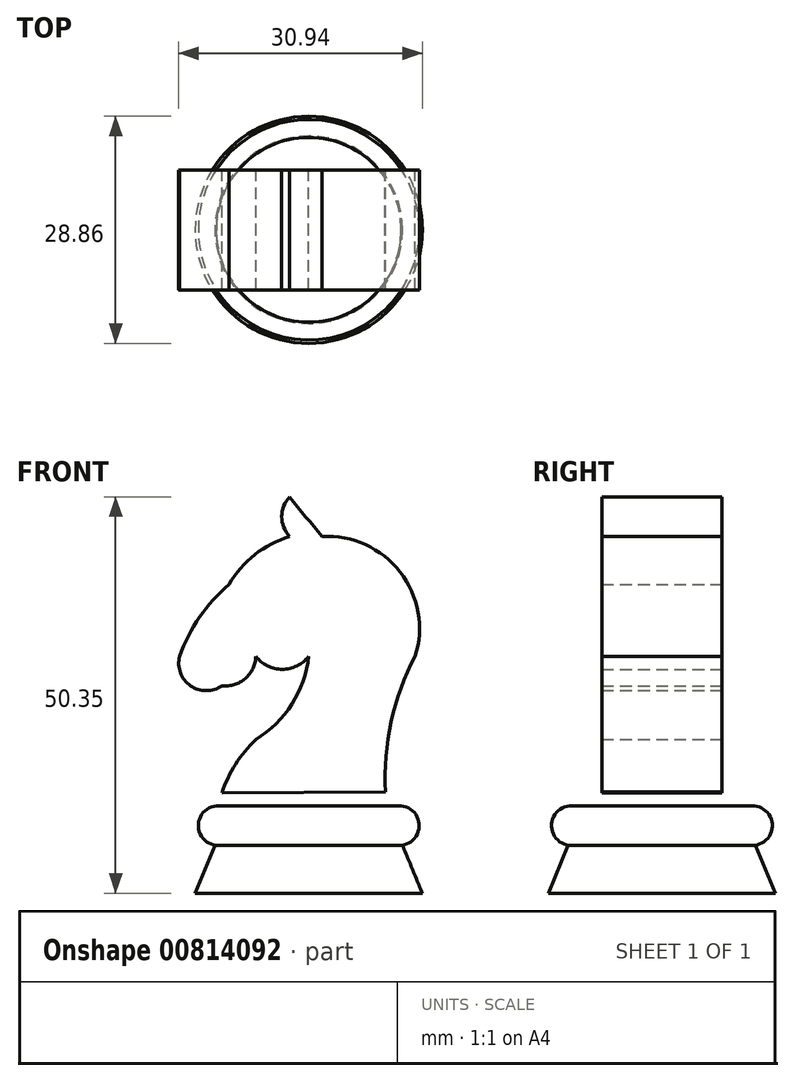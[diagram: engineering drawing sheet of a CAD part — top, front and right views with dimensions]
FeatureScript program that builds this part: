
annotation { "Feature Type Name" : "Feature", "Feature Type Description" : "" }
export const myFeature = defineFeature(function(context is Context, id is Id, definition is map)
    precondition{}
    {
        {
            var Q0;
            Q0=qCreatedBy(makeId("Front.planeOp"),FACE);
            var sketch = newSketch(context, id + "F0", { "sketchPlane" : qUnion([Q0])});
            skLineSegment(sketch, "E0", {"start": v(0, 0) * mm, "end": v(-14.43, 0) * mm});
            skLineSegment(sketch, "E1", {"start": v(-14.43, 0) * mm, "end": v(-11.92, 6.1) * mm});
            skLineSegment(sketch, "E2", {"start": v(-11.92, 6.1) * mm, "end": v(0, 6.1) * mm});
            skLineSegment(sketch, "E3", {"start": v(0, 6.1) * mm, "end": v(0, 0) * mm});
            skSolve(sketch);
        }
        {
            var Q0;
            Q0 = qSketchRegion(id + "F0", true);
            var Q1;
            Q1=sQuery(id+"F0.wireOp",EDGE,"E3");
            revolve(context, id + "F1", {"surfaceOperationType" : NewSurfaceOperationType.NEW, "entities" : qUnion([Q0]), "axis" : qUnion([Q1]), "revolveType" : RevolveType.FULL});
        }
        {
            var Q0;
            Q0=qCreatedBy(makeId("Front.planeOp"),FACE);
            var sketch = newSketch(context, id + "F2", { "sketchPlane" : qUnion([Q0])});
            skArc(sketch, "E4", {"start": v(-11.74, 11.11) * mm, "mid": v(-14, 8.33) * mm, "end": v(-11.2, 6.1) * mm});
            skLineSegment(sketch, "E5", {"start": v(-11.74, 11.11) * mm, "end": v(0, 11.11) * mm});
            skLineSegment(sketch, "E6", {"start": v(0, 11.11) * mm, "end": v(0, 5.73) * mm});
            skLineSegment(sketch, "E7", {"start": v(0, 5.73) * mm, "end": v(-11.2, 6.1) * mm});
            skSolve(sketch);
        }
        {
            var Q0;
            Q0 = qSketchRegion(id + "F2", true);
            var Q1;
            Q1=sQuery(id+"F2.wireOp",EDGE,"E6");
            revolve(context, id + "F3", {"operationType" : NewBodyOperationType.ADD, "surfaceOperationType" : NewSurfaceOperationType.NEW, "entities" : qUnion([Q0]), "axis" : qUnion([Q1]), "revolveType" : RevolveType.FULL});
        }
        {
            var Q0;
            Q0=qCreatedBy(makeId("Front.planeOp"),FACE);
            var sketch = newSketch(context, id + "F4", { "sketchPlane" : qUnion([Q0])});
            skArc(sketch, "E8", {"start": v(13.53, 30.1) * mm, "mid": v(10.47, 21.76) * mm, "end": v(9.77, 12.9) * mm});
            skArc(sketch, "E9", {"start": v(13.53, 30.1) * mm, "mid": v(11.6, 40.81) * mm, "end": v(1.7, 45.34) * mm});
            skArc(sketch, "E10", {"start": v(-2.42, 50.35) * mm, "mid": v(-0.38, 47.83) * mm, "end": v(1.7, 45.34) * mm});
            skArc(sketch, "E11", {"start": v(-2.42, 50.35) * mm, "mid": v(-3.43, 47.84) * mm, "end": v(-2.42, 45.34) * mm});
            skArc(sketch, "E12", {"start": v(-2.42, 45.34) * mm, "mid": v(-6.85, 43.01) * mm, "end": v(-10.12, 39.24) * mm});
            skArc(sketch, "E13", {"start": v(-10.12, 39.24) * mm, "mid": v(-13.85, 35.08) * mm, "end": v(-16.4, 30.1) * mm});
            skArc(sketch, "E14", {"start": v(-16.4, 30.1) * mm, "mid": v(-15, 26.36) * mm, "end": v(-11.02, 26.37) * mm});
            skArc(sketch, "E15", {"start": v(-11.02, 26.37) * mm, "mid": v(-8.04, 27.29) * mm, "end": v(-6.72, 30.1) * mm});
            skArc(sketch, "E16", {"start": v(-6.72, 30.1) * mm, "mid": v(-3.36, 28.45) * mm, "end": v(0, 30.1) * mm});
            skArc(sketch, "E17", {"start": v(-6.72, 19.53) * mm, "mid": v(-2.13, 24.04) * mm, "end": v(0, 30.1) * mm});
            skArc(sketch, "E18", {"start": v(-6.72, 19.53) * mm, "mid": v(-9.29, 16.4) * mm, "end": v(-11.02, 12.72) * mm});
            skLineSegment(sketch, "E19", {"start": v(-11.02, 12.72) * mm, "end": v(9.77, 12.9) * mm});
            skSolve(sketch);
        }
        {
            var Q0;
            Q0 = qSketchRegion(id + "F4", true);
            extrude(context, id + "F5", {"entities" : qUnion([Q0]), "depth" : 7.62 * mm, "offsetDistance" : 25.4 * mm});
        }
        {
            var Q0;
            Q0=makeQuery(id+"F5.opExtrude","CAP_FACE",FACE,{"disambiguationData":[OSD([sQuery(id+"F4.wireOp",EDGE,"E8"),sQuery(id+"F4.wireOp",EDGE,"E9"),sQuery(id+"F4.wireOp",EDGE,"E10"),sQuery(id+"F4.wireOp",EDGE,"E11"),sQuery(id+"F4.wireOp",EDGE,"E12"),sQuery(id+"F4.wireOp",EDGE,"E13"),sQuery(id+"F4.wireOp",EDGE,"E14"),sQuery(id+"F4.wireOp",EDGE,"E15"),sQuery(id+"F4.wireOp",EDGE,"E16"),sQuery(id+"F4.wireOp",EDGE,"E17"),sQuery(id+"F4.wireOp",EDGE,"E18"),sQuery(id+"F4.wireOp",EDGE,"E19")])],"isStart":false});
            extrude(context, id + "F6", {"entities" : qUnion([Q0]), "operationType" : NewBodyOperationType.ADD, "oppositeDirection" : true, "depth" : 15.24 * mm, "offsetDistance" : 25.4 * mm});
        }
    });
